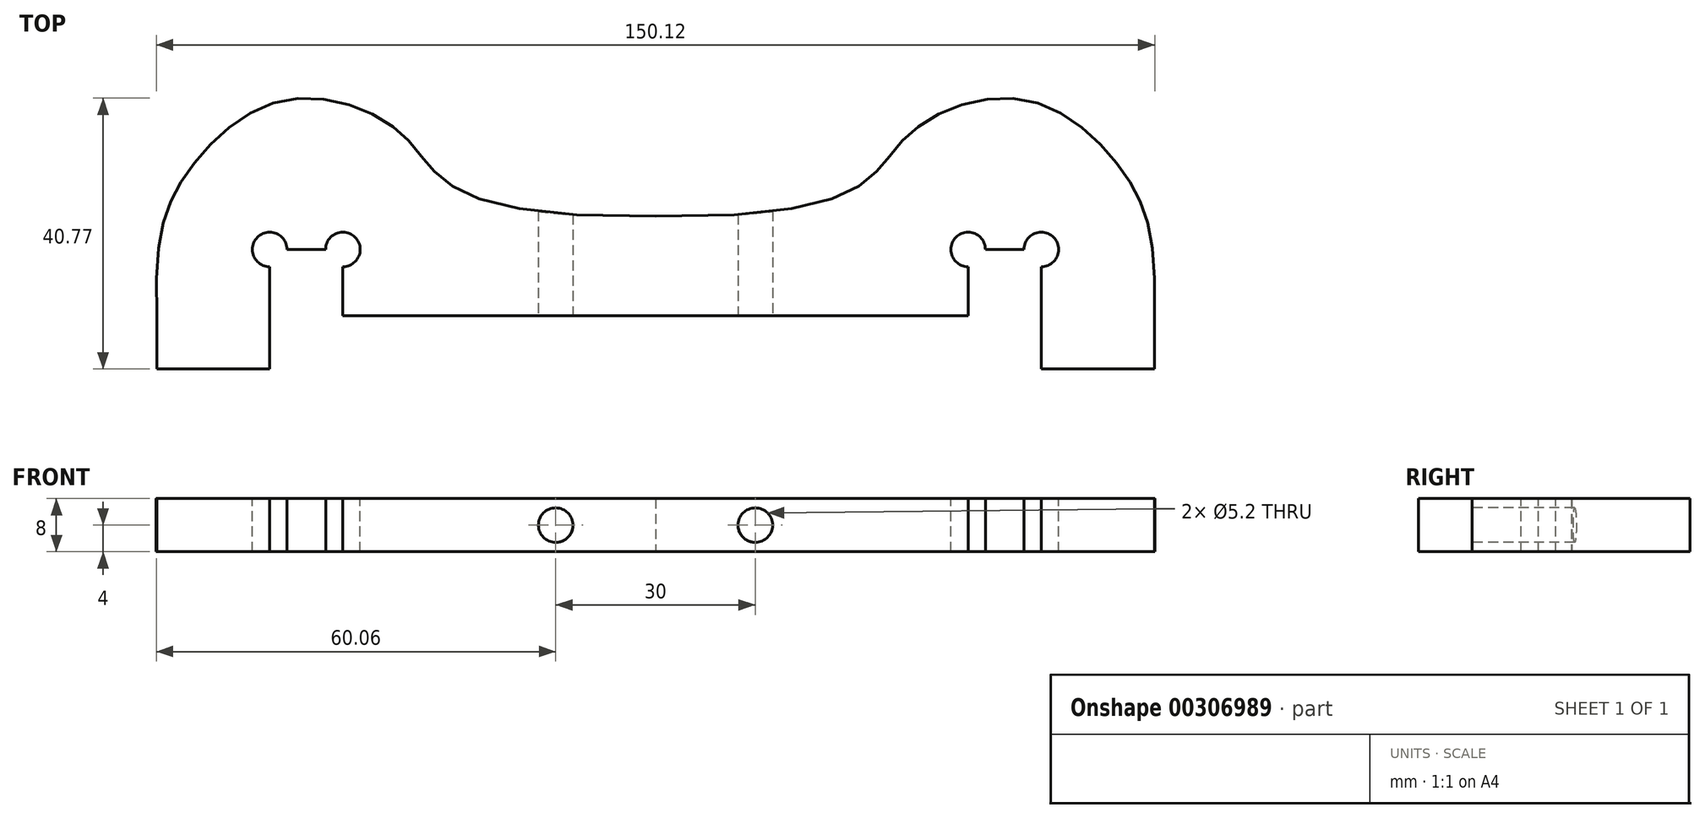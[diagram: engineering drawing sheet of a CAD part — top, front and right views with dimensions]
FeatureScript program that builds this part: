
annotation { "Feature Type Name" : "Feature", "Feature Type Description" : "" }
export const myFeature = defineFeature(function(context is Context, id is Id, definition is map)
    precondition{}
    {
        {
            var Q0;
            Q0=qCreatedBy(makeId("Top.planeOp"),FACE);
            var sketch = newSketch(context, id + "F0", { "sketchPlane" : qUnion([Q0])});
            skLineSegment(sketch, "E0", {"start": v(0, 0) * mm, "end": v(0, 15) * mm});
            skFitSpline(sketch, "E1", {"points": [v(0, 15) * mm, v(-38.02, 27.29) * mm, v(-55.34, 32.53) * mm, v(-70.32, 21.68) * mm, v(-75, 0) * mm], "startDerivative": vector(-314.64, -4.46) * mm, "endDerivative": vector(4.91, -142) * mm});
            skLineSegment(sketch, "E2", {"start": v(-75, 0) * mm, "end": v(0, 0) * mm});
            skSolve(sketch);
        }
        {
            var Q0;
            Q0 = qSketchRegion(id + "F0", true);
            extrude(context, id + "F1", {"entities" : qUnion([Q0]), "depth" : 8 * mm});
        }
        {
            var Q0;
            {var subQ0=makeQuery(id+"F1.opExtrude","SWEPT_FACE",FACE,{"disambiguationData":[OSD([sQuery(id+"F0.wireOp",EDGE,"E2")])]});Q0=makeQuery(id+"F8.boolean.opBoolean","MERGE",FACE,{"derivedFrom":[subQ0,makeQuery(id+"F8.opPattern","COPY",FACE,{"derivedFrom":subQ0,"instanceName":"1"})]});}
            var sketch = newSketch(context, id + "F2", { "sketchPlane" : qUnion([Q0])});
            skCircle(sketch, "E3", {"center": v(0, 4) * mm, "radius": 2.6 * mm});
            skLineSegment(sketch, "E4", {"start": v(0, -71.2) * mm, "end": v(0, 0) * mm, "construction": true});
            skCircle(sketch, "E5", {"center": v(-15, 4) * mm, "radius": 2.6 * mm});
            skCircle(sketch, "E6", {"center": v(15, 4) * mm, "radius": 2.6 * mm});
            skSolve(sketch);
        }
        {
            var Q0;
            Q0=makeQuery(id+"F2.imprint","IMPRINT",FACE,{"disambiguationData":[TD([[makeQuery(id+"F2.imprint","IMPRINT",EDGE,{"derivedFrom":sQuery(id+"F2.wireOp",EDGE,"E5")}),1.0]])]});
            var Q1;
            Q1=makeQuery(id+"F2.imprint","IMPRINT",FACE,{"disambiguationData":[TD([[makeQuery(id+"F2.imprint","IMPRINT",EDGE,{"derivedFrom":sQuery(id+"F2.wireOp",EDGE,"E6")}),1.0]])]});
            extrude(context, id + "F3", {"entities" : qUnion([Q0, Q1]), "operationType" : NewBodyOperationType.REMOVE, "endBound" : BoundingType.THROUGH_ALL, "oppositeDirection" : true, "depth" : 25 * mm});
        }
        {
            var Q0;
            {var subQ0=makeQuery(id+"F1.opExtrude","SWEPT_FACE",FACE,{"disambiguationData":[OSD([sQuery(id+"F0.wireOp",EDGE,"E2")])]});Q0=makeQuery(id+"F8.boolean.opBoolean","MERGE",FACE,{"derivedFrom":[subQ0,makeQuery(id+"F8.opPattern","COPY",FACE,{"derivedFrom":subQ0,"instanceName":"1"})]});}
            var sketch = newSketch(context, id + "F4", { "sketchPlane" : qUnion([Q0])});
            skLineSegment(sketch, "E7", {"start": v(0, 0) * mm, "end": v(-58, 0) * mm});
            skLineSegment(sketch, "E8", {"start": v(-58, 0) * mm, "end": v(-58, 8) * mm});
            skLineSegment(sketch, "E9", {"start": v(-37.5, 8) * mm, "end": v(-58, 8) * mm});
            skLineSegment(sketch, "E10", {"start": v(-58, 0) * mm, "end": v(-75, 0) * mm});
            skLineSegment(sketch, "E11", {"start": v(-75, 0) * mm, "end": v(-75, 8) * mm});
            skLineSegment(sketch, "E12", {"start": v(-75, 8) * mm, "end": v(-58, 8) * mm});
            skSolve(sketch);
        }
        {
            var Q0;
            Q0=makeQuery(id+"F4.imprint","IMPRINT",FACE,{"disambiguationData":[TD([[makeQuery(id+"F4.imprint","IMPRINT",EDGE,{"derivedFrom":sQuery(id+"F4.wireOp",EDGE,"E8")}),1.0]])]});
            extrude(context, id + "F5", {"entities" : qUnion([Q0]), "operationType" : NewBodyOperationType.ADD, "depth" : 8 * mm});
        }
        {
            var Q0;
            {var subQ0=makeQuery(id+"F1.opExtrude","SWEPT_FACE",FACE,{"disambiguationData":[OSD([sQuery(id+"F0.wireOp",EDGE,"E2")])]});Q0=makeQuery(id+"F8.boolean.opBoolean","MERGE",FACE,{"derivedFrom":[subQ0,makeQuery(id+"F8.opPattern","COPY",FACE,{"derivedFrom":subQ0,"instanceName":"1"})]});}
            var sketch = newSketch(context, id + "F6", { "sketchPlane" : qUnion([Q0])});
            skLineSegment(sketch, "E13.bottom", {"start": v(-58, 8) * mm, "end": v(-47, 8) * mm});
            skLineSegment(sketch, "E13.top", {"start": v(-58, 0) * mm, "end": v(-47, 0) * mm});
            skLineSegment(sketch, "E13.left", {"start": v(-58, 8) * mm, "end": v(-58, 0) * mm});
            skLineSegment(sketch, "E13.right", {"start": v(-47, 8) * mm, "end": v(-47, 0) * mm});
            skSolve(sketch);
        }
        {
            var Q0;
            Q0=makeQuery(id+"F6.imprint","IMPRINT",FACE,{"disambiguationData":[TD([[makeQuery(id+"F6.imprint","IMPRINT",EDGE,{"derivedFrom":sQuery(id+"F6.wireOp",EDGE,"E13.bottom")}),-1.0]])]});
            extrude(context, id + "F7", {"entities" : qUnion([Q0]), "operationType" : NewBodyOperationType.REMOVE, "oppositeDirection" : true, "depth" : 10 * mm});
        }
        {
            var Q0;
            Q0=makeQuery(id+"F1.opExtrude","SWEPT_BODY",BODY,{"disambiguationData":[OSD([sQuery(id+"F0.wireOp",EDGE,"E0"),sQuery(id+"F0.wireOp",EDGE,"E1"),sQuery(id+"F0.wireOp",EDGE,"E2")])]});
            var Q1;
            Q1=makeQuery(id+"F1.opExtrude","SWEPT_FACE",FACE,{"disambiguationData":[OSD([sQuery(id+"F0.wireOp",EDGE,"E0")])]});
            mirror(context, id + "F8", {"operationType" : NewBodyOperationType.ADD, "entities" : qUnion([Q0]), "mirrorPlane" : qUnion([Q1])});
        }
        {
            var Q0;
            {var subQ0=makeQuery(id+"F1.opExtrude","CAP_FACE",FACE,{"disambiguationData":[OSD([sQuery(id+"F0.wireOp",EDGE,"E0"),sQuery(id+"F0.wireOp",EDGE,"E1"),sQuery(id+"F0.wireOp",EDGE,"E2")])],"isStart":false});Q0=makeQuery(id+"F5.boolean.opBoolean","MERGE",FACE,{"derivedFrom":[makeQuery(id+"F8.boolean.opBoolean","MERGE",FACE,{"derivedFrom":[subQ0,makeQuery(id+"F8.opPattern","COPY",FACE,{"derivedFrom":subQ0,"instanceName":"1"})]}),makeQuery(id+"F5.opExtrude","SWEPT_FACE",FACE,{"disambiguationData":[OSD([sQuery(id+"F4.wireOp",EDGE,"E12")])]})]});}
            var sketch = newSketch(context, id + "F9", { "sketchPlane" : qUnion([Q0])});
            skCircle(sketch, "E14", {"center": v(58, 10) * mm, "radius": 2.6 * mm});
            skCircle(sketch, "E15", {"center": v(47, 10) * mm, "radius": 2.6 * mm});
            skCircle(sketch, "E16", {"center": v(-47, 10) * mm, "radius": 2.6 * mm});
            skCircle(sketch, "E17", {"center": v(-58, 10) * mm, "radius": 2.6 * mm});
            skSolve(sketch);
        }
        {
            var Q0;
            {var subQ0=sQuery(id+"F9.wireOp",EDGE,"E14");var subQ1=sQuery(id+"F6.wireOp",EDGE,"E13.bottom");var subQ4=makeQuery(id+"F8.opPattern","COPY",EDGE,{"derivedFrom":makeQuery(id+"F7.boolean.opBoolean","COPY",EDGE,{"derivedFrom":makeQuery(id+"F7.opExtrude","CAP_EDGE",EDGE,{"disambiguationData":[OSD([subQ1])],"isStart":false})}),"instanceName":"1"});var subQ5=makeQuery(id+"F9.imprint","INTERSECT",VERTEX,{"derivedFrom":[subQ4,subQ0]});Q0=makeQuery(id+"F9.imprint","IMPRINT",FACE,{"disambiguationData":[TD([[makeQuery(id+"F9.imprint","IMPRINT",EDGE,{"disambiguationData":[TD([[subQ5,1.0]])],"derivedFrom":subQ0}),1.0]])]});}
            var Q1;
            {var subQ0=sQuery(id+"F9.wireOp",EDGE,"E15");var subQ1=sQuery(id+"F6.wireOp",EDGE,"E13.bottom");var subQ4=makeQuery(id+"F8.opPattern","COPY",EDGE,{"derivedFrom":makeQuery(id+"F7.boolean.opBoolean","COPY",EDGE,{"derivedFrom":makeQuery(id+"F7.opExtrude","CAP_EDGE",EDGE,{"disambiguationData":[OSD([subQ1])],"isStart":false})}),"instanceName":"1"});var subQ5=makeQuery(id+"F9.imprint","INTERSECT",VERTEX,{"derivedFrom":[subQ4,subQ0]});Q1=makeQuery(id+"F9.imprint","IMPRINT",FACE,{"disambiguationData":[TD([[makeQuery(id+"F9.imprint","IMPRINT",EDGE,{"disambiguationData":[TD([[subQ5,-1.0]])],"derivedFrom":subQ0}),1.0]])]});}
            var Q2;
            {var subQ0=sQuery(id+"F9.wireOp",EDGE,"E16");var subQ1=sQuery(id+"F6.wireOp",EDGE,"E13.bottom");var subQ4=makeQuery(id+"F7.boolean.opBoolean","COPY",EDGE,{"derivedFrom":makeQuery(id+"F7.opExtrude","CAP_EDGE",EDGE,{"disambiguationData":[OSD([subQ1])],"isStart":false})});var subQ5=makeQuery(id+"F9.imprint","INTERSECT",VERTEX,{"derivedFrom":[subQ4,subQ0]});Q2=makeQuery(id+"F9.imprint","IMPRINT",FACE,{"disambiguationData":[TD([[makeQuery(id+"F9.imprint","IMPRINT",EDGE,{"disambiguationData":[TD([[subQ5,1.0]])],"derivedFrom":subQ0}),1.0]])]});}
            var Q3;
            {var subQ0=sQuery(id+"F9.wireOp",EDGE,"E17");var subQ1=sQuery(id+"F6.wireOp",EDGE,"E13.bottom");var subQ4=makeQuery(id+"F7.boolean.opBoolean","COPY",EDGE,{"derivedFrom":makeQuery(id+"F7.opExtrude","CAP_EDGE",EDGE,{"disambiguationData":[OSD([subQ1])],"isStart":false})});var subQ5=makeQuery(id+"F9.imprint","INTERSECT",VERTEX,{"derivedFrom":[subQ4,subQ0]});Q3=makeQuery(id+"F9.imprint","IMPRINT",FACE,{"disambiguationData":[TD([[makeQuery(id+"F9.imprint","IMPRINT",EDGE,{"disambiguationData":[TD([[subQ5,-1.0]])],"derivedFrom":subQ0}),1.0]])]});}
            extrude(context, id + "F10", {"entities" : qUnion([Q0, Q1, Q2, Q3]), "operationType" : NewBodyOperationType.REMOVE, "endBound" : BoundingType.THROUGH_ALL, "oppositeDirection" : true, "depth" : 25 * mm});
        }
    });
